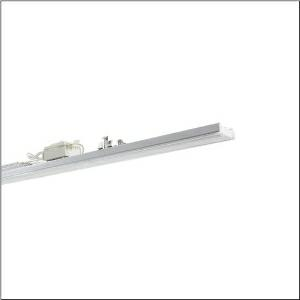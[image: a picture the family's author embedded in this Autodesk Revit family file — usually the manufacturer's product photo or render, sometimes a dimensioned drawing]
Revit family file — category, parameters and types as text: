
# Revit family: licross_r__21_recessed_mo_52tl12dn395g_c848
name_source: partatom
category: Lighting Fixtures
units: mm (PartAtom-declared; Revit-internal decimal feet)

## family parameters
Cut with Voids When Loaded = No
Host = Face
Light Source = No
Part Type = Normal
Room Calculation Point = No
Round Connector Dimension = Use Diameter
Shared = No

## types (1)
- --- (1 x LED, 9630 lm, 58 W, 3000K)
    Apparent Load = 58 VA
    CIE Flux Codes = 72 92 99 100 100
    Color Rendering = 80
    Color Temperature = 3000K
    Default Elevation = 1800 mm
    Description = Licross® 21 Recessed MO, luminaire insert, of sheet steel, galvanised, coil coated, white, length: 1.500mm, width: 66mm, height: 67mm, LED rated luminous flux: 9.630lm, light colour: 830, control gear: DALI 2, with plug, 5-pole, with phase selection, mains connection: 220..240V, AC, 50/60Hz, rated input power: 58W, halogen-free wiring, primary optical cover: cover, of PMMA, light emission: direct distribution, primary light characteristic: symmetric, protection rating (complete): IP40, insulation class (complete): insulation class I (protective earthing), certification: CE, ENEC, VDE, UKCA, protection symbol: D if used in an environment without relevant dust loads with corresponding accessories, impact resistance: IK06, permissible ambient temperature for indoor applications: -25..+35°C, corresponds to IFS (International Featured Standards) requirements for safety and quality in the food industry, reducing of maximum allowable ambient temperature of 5°C with ceiling mounting, LABS conformity tested according to VDMA 24364:2018-05, packaging unit: 1 piece
    Height = 58 mm
    Lamp = 1 x LED
    Lamp Light Flux = 9630 lm
    Lamp Power = 58 W
    Lamp count = 1
    Length = 1500 mm
    Luminous efficacy = 166 lm/W
    Manufacturer = Siteco
    ModVariant = No
    Model = 52TL12DN395G
    Mounting Place = Ceiling
    Mounting Type = Pendant
    Number of Poles = 1
    OnlyDefault = Yes
    Power Factor = 1
    Product Name = Licross® 21 Recessed MO
    Product group = luminaire insert
    ProductGroupID = 902
    Protection Class = Protection class I
    Protection Degree = IP 40
    RLX_Detail_Level = 1
    RLX_Emergency_Light_Flux = 0 lm
    RLX_Emergency_Type = 0
    RLX_Emergency_Type_DB = No
    RlxData = <blob elided: 24569 chars, md5=3ccdb48f>
    Socket = socket
    Standby Power = 0 W
    System Light Flux = 9630 lm
    System Power = 58 W
    Type Comments = factory setting: luminous flux: 100 % | dim-lin: 254 | 390 mA
    Type Image = l_1296930.jpg
    URL = http://relux.com
    VarID = @adj_089656
    Voltage = 0 V
    Weight = 0.00 kg
    Width = 66 mm

## geometry (parser evidence)
native form markers: Blend x4, Sweep x10
no freeform markers — native parametric forms only
